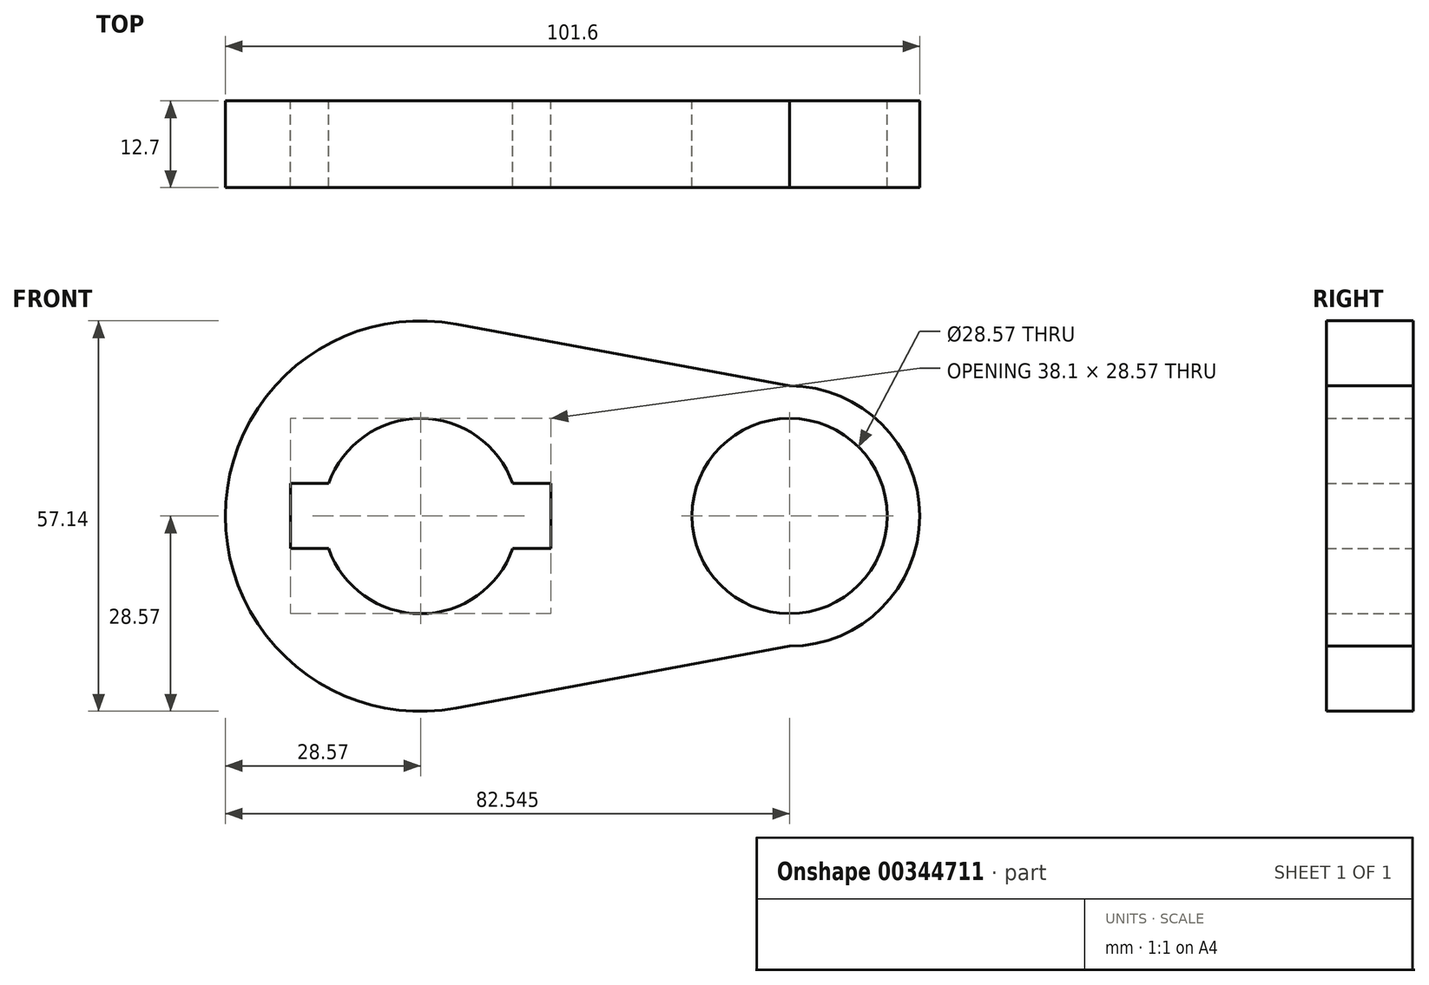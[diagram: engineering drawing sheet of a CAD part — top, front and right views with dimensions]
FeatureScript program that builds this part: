
annotation { "Feature Type Name" : "Feature", "Feature Type Description" : "" }
export const myFeature = defineFeature(function(context is Context, id is Id, definition is map)
    precondition{}
    {
        {
            var Q0;
            Q0=qCreatedBy(makeId("Front.planeOp"),FACE);
            var sketch = newSketch(context, id + "F0", { "sketchPlane" : qUnion([Q0])});
            skCircle(sketch, "E0", {"center": v(0, 0) * mm, "radius": 28.58 * mm});
            skCircle(sketch, "E1", {"center": v(53.98, 0) * mm, "radius": 19.05 * mm});
            skLineSegment(sketch, "E2", {"start": v(5.21, 28.1) * mm, "end": v(53.98, 19.05) * mm});
            skLineSegment(sketch, "E3", {"start": v(53.98, -19.05) * mm, "end": v(5.21, -28.1) * mm});
            skCircle(sketch, "E4", {"center": v(0, 0) * mm, "radius": 14.29 * mm});
            skCircle(sketch, "E5", {"center": v(53.98, 0) * mm, "radius": 14.29 * mm});
            skLineSegment(sketch, "E6.bottom", {"start": v(19.05, -4.76) * mm, "end": v(-19.05, -4.76) * mm});
            skLineSegment(sketch, "E6.top", {"start": v(19.05, 4.76) * mm, "end": v(-19.05, 4.76) * mm});
            skLineSegment(sketch, "E6.left", {"start": v(19.05, -4.76) * mm, "end": v(19.05, 4.76) * mm});
            skLineSegment(sketch, "E6.right", {"start": v(-19.05, -4.76) * mm, "end": v(-19.05, 4.76) * mm});
            skSolve(sketch);
        }
        {
            var Q0;
            {var subQ7=sQuery(id+"F0.wireOp",EDGE,"E6.left");Q0=makeQuery(id+"F0.imprint","IMPRINT",FACE,{"disambiguationData":[TD([[makeQuery(id+"F0.imprint","IMPRINT",EDGE,{"derivedFrom":subQ7}),-1.0]])]});}
            var Q1;
            {var subQ0=sQuery(id+"F0.wireOp",EDGE,"E2");Q1=makeQuery(id+"F0.imprint","IMPRINT",FACE,{"disambiguationData":[TD([[makeQuery(id+"F0.imprint","IMPRINT",EDGE,{"derivedFrom":subQ0}),-1.0]])]});}
            var Q2;
            Q2=makeQuery(id+"F0.imprint","IMPRINT",FACE,{"disambiguationData":[TD([[makeQuery(id+"F0.imprint","IMPRINT",EDGE,{"derivedFrom":sQuery(id+"F0.wireOp",EDGE,"E5")}),-1.0]])]});
            extrude(context, id + "F1", {"entities" : qUnion([Q0, Q1, Q2]), "depth" : 12.7 * mm, "offsetDistance" : 25.4 * mm});
        }
    });
